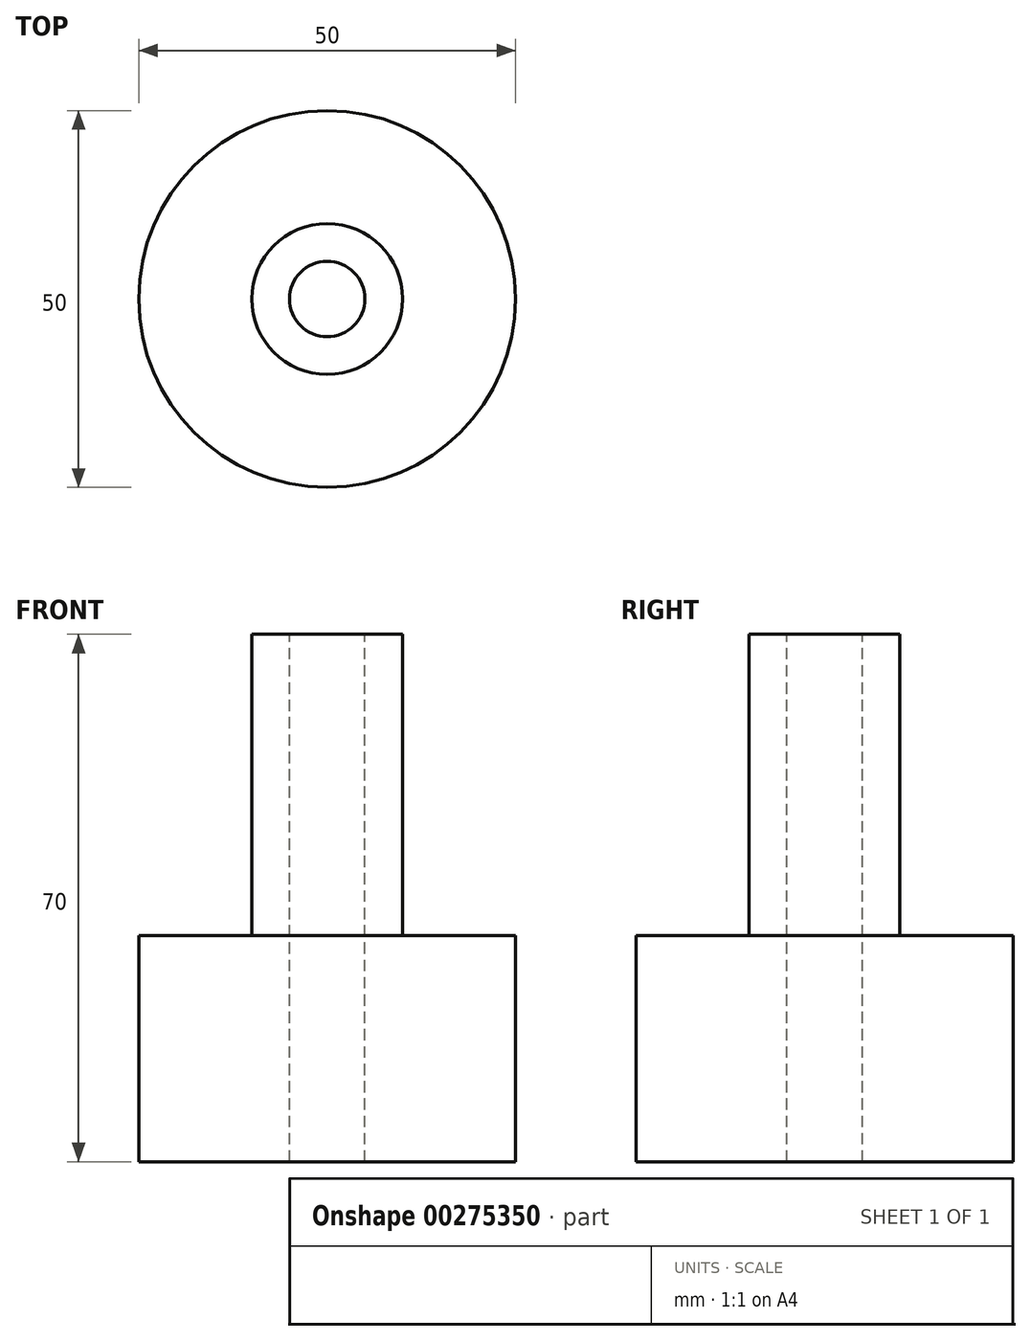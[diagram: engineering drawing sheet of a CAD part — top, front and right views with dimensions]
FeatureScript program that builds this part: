
annotation { "Feature Type Name" : "Feature", "Feature Type Description" : "" }
export const myFeature = defineFeature(function(context is Context, id is Id, definition is map)
    precondition{}
    {
        {
            var Q0;
            Q0=qCreatedBy(makeId("Top.planeOp"),FACE);
            var sketch = newSketch(context, id + "F0", { "sketchPlane" : qUnion([Q0])});
            skCircle(sketch, "E0", {"center": v(0, 0) * mm, "radius": 25 * mm});
            skSolve(sketch);
        }
        {
            var Q0;
            Q0 = qSketchRegion(id + "F0", true);
            extrude(context, id + "F1", {"entities" : qUnion([Q0]), "depth" : 30 * mm});
        }
        {
            var Q0;
            Q0=makeQuery(id+"F1.opExtrude","CAP_FACE",FACE,{"disambiguationData":[OSD([sQuery(id+"F0.wireOp",EDGE,"E0")])],"isStart":false});
            var sketch = newSketch(context, id + "F2", { "sketchPlane" : qUnion([Q0])});
            skCircle(sketch, "E1", {"center": v(0, 0) * mm, "radius": 10 * mm});
            skSolve(sketch);
        }
        {
            var Q0;
            Q0 = qSketchRegion(id + "F2", true);
            extrude(context, id + "F3", {"entities" : qUnion([Q0]), "operationType" : NewBodyOperationType.ADD, "depth" : 40 * mm});
        }
        {
            var Q0;
            Q0=makeQuery(id+"F3.opExtrude","CAP_FACE",FACE,{"disambiguationData":[OSD([sQuery(id+"F2.wireOp",EDGE,"E1")])],"isStart":false});
            var sketch = newSketch(context, id + "F4", { "sketchPlane" : qUnion([Q0])});
            skCircle(sketch, "E2", {"center": v(0, 0) * mm, "radius": 5 * mm});
            skSolve(sketch);
        }
        {
            var Q0;
            Q0=makeQuery(id+"F4.imprint","IMPRINT",FACE,{"disambiguationData":[TD([[makeQuery(id+"F4.imprint","IMPRINT",EDGE,{"derivedFrom":sQuery(id+"F4.wireOp",EDGE,"E2")}),1.0]])]});
            var Q1;
            Q1=makeQuery(id+"F1.opExtrude","CAP_FACE",FACE,{"disambiguationData":[OSD([sQuery(id+"F0.wireOp",EDGE,"E0")])],"isStart":true});
            extrude(context, id + "F5", {"entities" : qUnion([Q0, Q1]), "operationType" : NewBodyOperationType.REMOVE, "endBound" : BoundingType.THROUGH_ALL, "oppositeDirection" : true, "depth" : 74 * mm});
        }
    });
